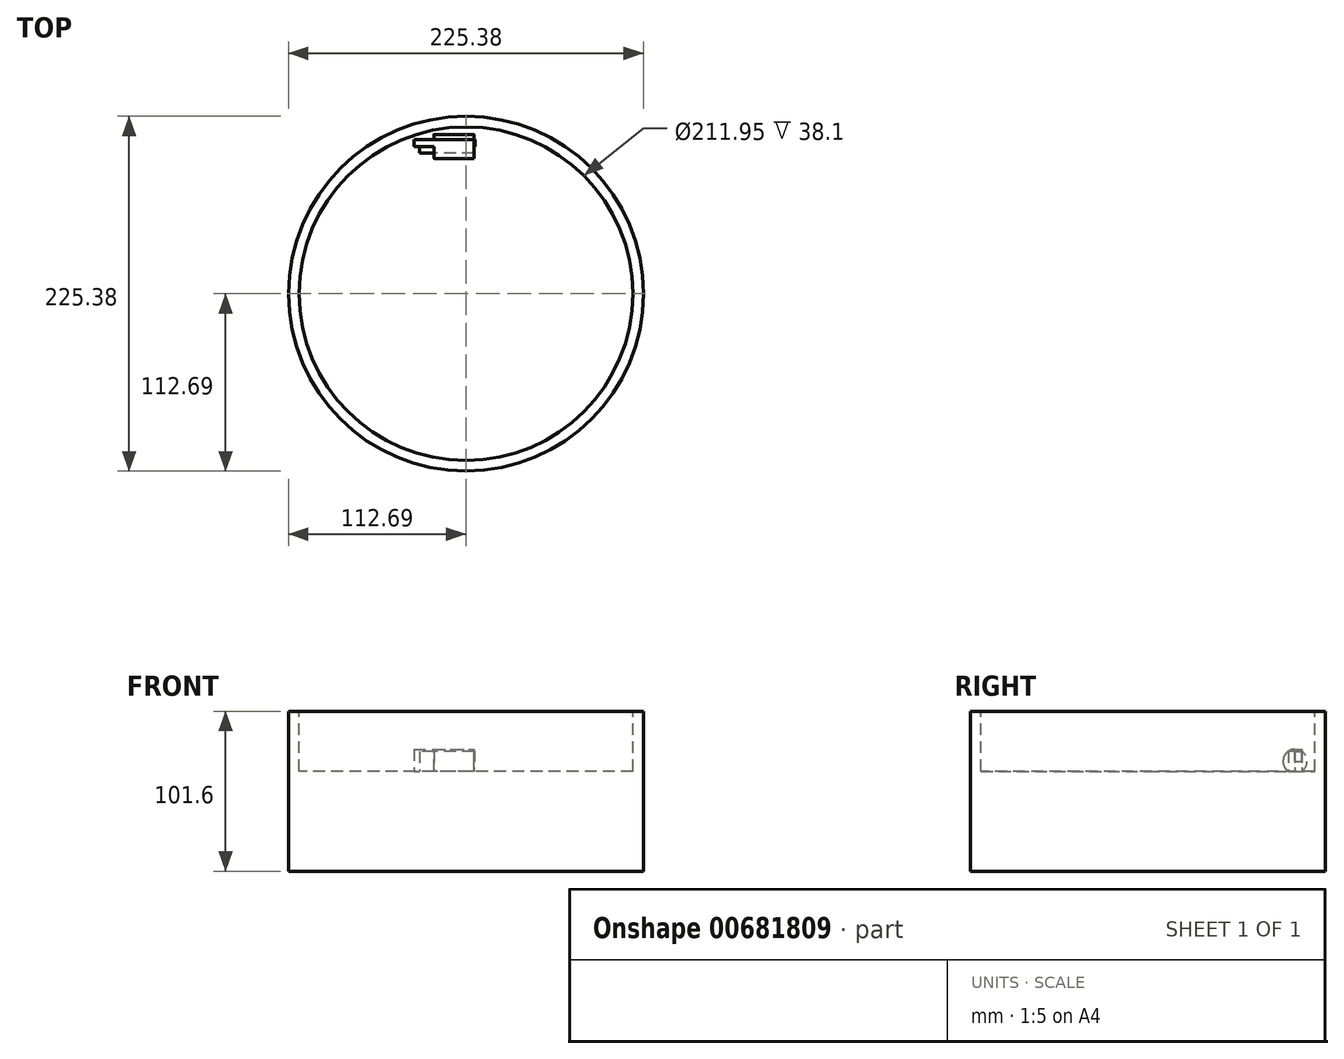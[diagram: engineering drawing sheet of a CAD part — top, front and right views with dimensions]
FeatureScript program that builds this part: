
annotation { "Feature Type Name" : "Feature", "Feature Type Description" : "" }
export const myFeature = defineFeature(function(context is Context, id is Id, definition is map)
    precondition{}
    {
        {
            var Q0;
            Q0=qCreatedBy(makeId("Top.planeOp"),FACE);
            var sketch = newSketch(context, id + "F0", { "sketchPlane" : qUnion([Q0])});
            skCircle(sketch, "E0", {"center": v(0, 0) * mm, "radius": 112.69 * mm});
            skSolve(sketch);
        }
        {
            var Q0;
            Q0 = qSketchRegion(id + "F0", true);
            extrude(context, id + "F1", {"entities" : qUnion([Q0]), "depth" : 101.6 * mm, "offsetDistance" : 25.4 * mm});
        }
        {
            var Q0;
            Q0=makeQuery(id+"F1.opExtrude","CAP_FACE",FACE,{"disambiguationData":[OSD([sQuery(id+"F0.wireOp",EDGE,"E0")])],"isStart":false});
            var sketch = newSketch(context, id + "F2", { "sketchPlane" : qUnion([Q0])});
            skCircle(sketch, "E1", {"center": v(0, 0) * mm, "radius": 105.97 * mm});
            skSolve(sketch);
        }
        {
            var Q0;
            Q0 = qSketchRegion(id + "F2", true);
            extrude(context, id + "F3", {"entities" : qUnion([Q0]), "operationType" : NewBodyOperationType.REMOVE, "oppositeDirection" : true, "depth" : 88.9 * mm, "offsetDistance" : 25.4 * mm});
        }
        {
            var Q0;
            Q0=makeQuery(id+"F3.boolean.opBoolean","COPY",FACE,{"derivedFrom":makeQuery(id+"F3.opExtrude","CAP_FACE",FACE,{"disambiguationData":[OSD([sQuery(id+"F2.wireOp",EDGE,"E1")])],"isStart":false})});
            extrude(context, id + "F4", {"entities" : qUnion([Q0]), "operationType" : NewBodyOperationType.ADD, "depth" : 25.4 * mm, "offsetDistance" : 25.4 * mm});
        }
        {
            var Q0;
            Q0=makeQuery(id+"F4.opExtrude","CAP_FACE",FACE,{"disambiguationData":[OSD([sQuery(id+"F2.wireOp",EDGE,"E1")])],"isStart":false});
            extrude(context, id + "F5", {"entities" : qUnion([Q0]), "operationType" : NewBodyOperationType.ADD, "depth" : 25.4 * mm, "offsetDistance" : 25.4 * mm});
        }
        {
            var Q0;
            Q0=makeQuery(id+"F5.opExtrude","CAP_FACE",FACE,{"disambiguationData":[OSD([sQuery(id+"F2.wireOp",EDGE,"E1")])],"isStart":false});
            var sketch = newSketch(context, id + "F6", { "sketchPlane" : qUnion([Q0])});
            skLineSegment(sketch, "E2.bottom", {"start": v(-20.31, 97.75) * mm, "end": v(-29.58, 97.75) * mm});
            skLineSegment(sketch, "E2.top", {"start": v(-20.31, 89.28) * mm, "end": v(-29.58, 89.28) * mm});
            skLineSegment(sketch, "E2.left", {"start": v(-20.31, 97.75) * mm, "end": v(-20.31, 89.28) * mm});
            skLineSegment(sketch, "E2.right", {"start": v(-29.58, 97.75) * mm, "end": v(-29.58, 89.28) * mm});
            skSolve(sketch);
        }
        {
            var Q0;
            Q0 = qSketchRegion(id + "F6", true);
            extrude(context, id + "F7", {"entities" : qUnion([Q0]), "operationType" : NewBodyOperationType.ADD, "depth" : 12.7 * mm, "offsetDistance" : 25.4 * mm});
        }
        {
            var Q0;
            Q0=makeQuery(id+"F7.opExtrude","SWEPT_FACE",FACE,{"disambiguationData":[OSD([sQuery(id+"F6.wireOp",EDGE,"E2.left")])]});
            var sketch = newSketch(context, id + "F8", { "sketchPlane" : qUnion([Q0])});
            skCircle(sketch, "E3", {"center": v(93.52, 69.85) * mm, "radius": 7.63 * mm});
            skPoint(sketch, "E3.centerSnap0", {"position": v(89.28, 69.85) * mm});
            skPoint(sketch, "E3.centerSnap1", {"position": v(93.52, 63.5) * mm});
            skSolve(sketch);
        }
        {
            var Q0;
            Q0 = qSketchRegion(id + "F8", true);
            extrude(context, id + "F9", {"entities" : qUnion([Q0]), "operationType" : NewBodyOperationType.ADD, "depth" : 25.4 * mm, "offsetDistance" : 25.4 * mm});
        }
        {
            var Q0;
            Q0=makeQuery(id+"F9.opExtrude","CAP_FACE",FACE,{"disambiguationData":[OSD([sQuery(id+"F8.wireOp",EDGE,"E3")])],"isStart":false});
            var sketch = newSketch(context, id + "F10", { "sketchPlane" : qUnion([Q0])});
            skLineSegment(sketch, "E4.bottom", {"start": v(93.52, 77.48) * mm, "end": v(97.75, 77.48) * mm});
            skLineSegment(sketch, "E4.top", {"start": v(93.52, 63.5) * mm, "end": v(97.75, 63.5) * mm});
            skLineSegment(sketch, "E4.left", {"start": v(93.52, 77.48) * mm, "end": v(93.52, 63.5) * mm});
            skLineSegment(sketch, "E4.right", {"start": v(97.75, 77.48) * mm, "end": v(97.75, 63.5) * mm});
            skSolve(sketch);
        }
        {
            var Q0;
            Q0 = qSketchRegion(id + "F10", true);
            extrude(context, id + "F11", {"entities" : qUnion([Q0]), "operationType" : NewBodyOperationType.ADD, "oppositeDirection" : true, "depth" : 38.1 * mm, "offsetDistance" : 25.4 * mm});
        }
        {
            var Q0;
            Q0=makeQuery(id+"F11.boolean.opBoolean","MERGE",FACE,{"derivedFrom":[makeQuery(id+"F9.opExtrude","CAP_FACE",FACE,{"disambiguationData":[OSD([sQuery(id+"F8.wireOp",EDGE,"E3")])],"isStart":false}),makeQuery(id+"F11.opExtrude","CAP_FACE",FACE,{"disambiguationData":[OSD([sQuery(id+"F10.wireOp",EDGE,"E4.bottom"),sQuery(id+"F10.wireOp",EDGE,"E4.top"),sQuery(id+"F10.wireOp",EDGE,"E4.left"),sQuery(id+"F10.wireOp",EDGE,"E4.right")])],"isStart":true})]});
            var sketch = newSketch(context, id + "F12", { "sketchPlane" : qUnion([Q0])});
            skLineSegment(sketch, "E5.bottom", {"start": v(93.52, 69.85) * mm, "end": v(97.75, 69.85) * mm});
            skLineSegment(sketch, "E5.top", {"start": v(93.52, 76.2) * mm, "end": v(97.75, 76.2) * mm});
            skLineSegment(sketch, "E5.left", {"start": v(93.52, 69.85) * mm, "end": v(93.52, 76.2) * mm});
            skLineSegment(sketch, "E5.right", {"start": v(97.75, 69.85) * mm, "end": v(97.75, 76.2) * mm});
            skSolve(sketch);
        }
        {
            var Q0;
            Q0 = qSketchRegion(id + "F12", true);
            extrude(context, id + "F13", {"entities" : qUnion([Q0]), "operationType" : NewBodyOperationType.ADD, "depth" : 0.76 * mm, "offsetDistance" : 25.4 * mm});
        }
    });
